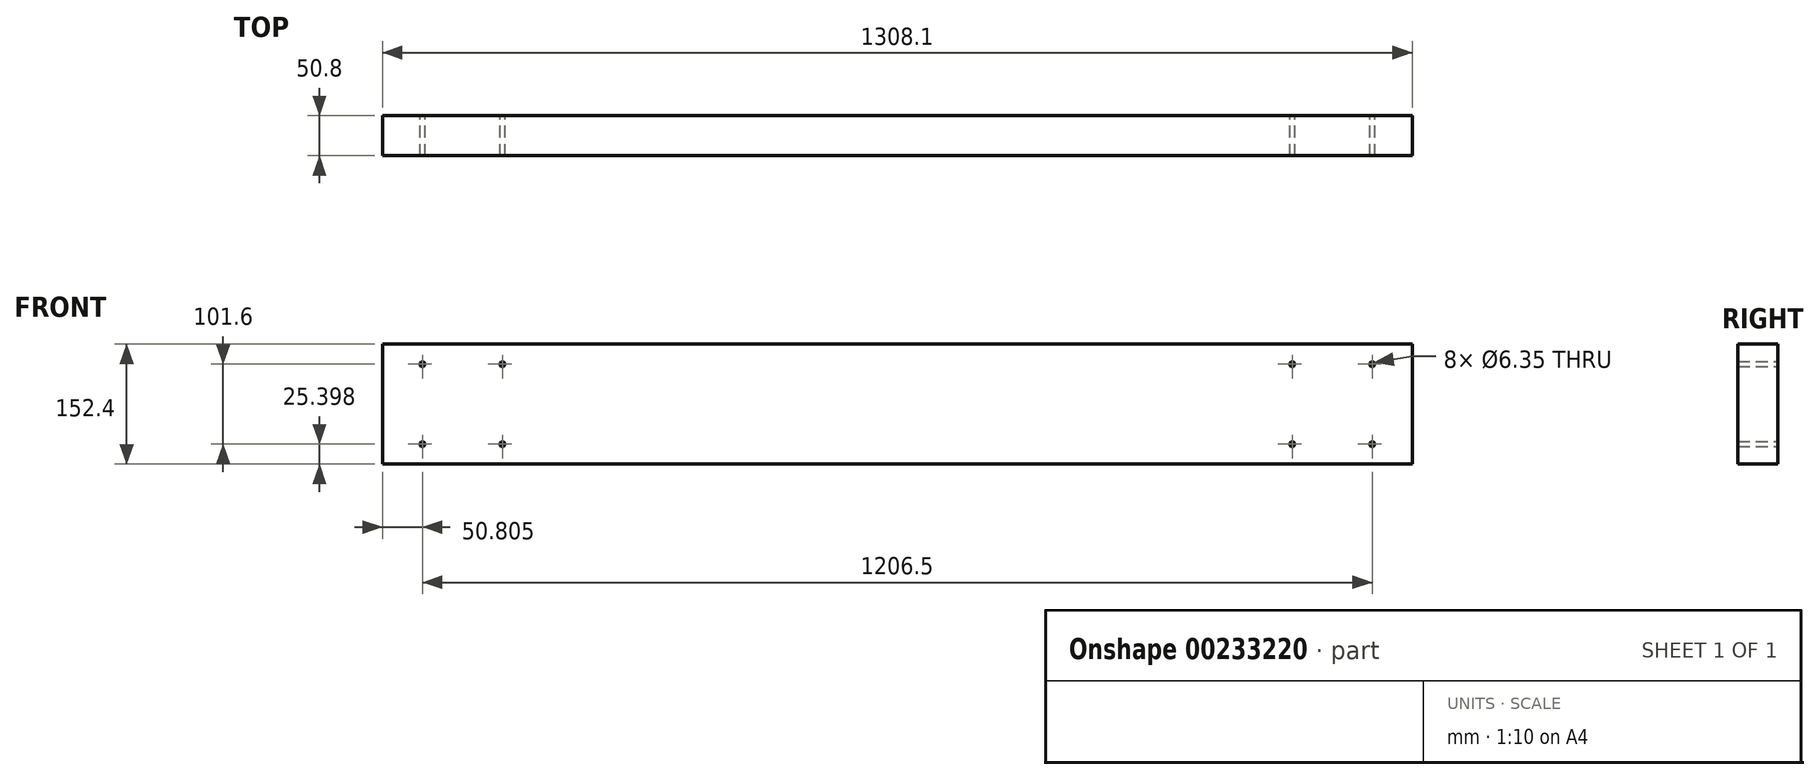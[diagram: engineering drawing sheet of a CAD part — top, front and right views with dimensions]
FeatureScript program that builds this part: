
annotation { "Feature Type Name" : "Feature", "Feature Type Description" : "" }
export const myFeature = defineFeature(function(context is Context, id is Id, definition is map)
    precondition{}
    {
        {
            var Q0;
            Q0=qCreatedBy(makeId("Front.planeOp"),FACE);
            var sketch = newSketch(context, id + "F0", { "sketchPlane" : qUnion([Q0])});
            skLineSegment(sketch, "E0.bottom", {"start": v(-533.62, -477.17) * mm, "end": v(774.48, -477.17) * mm});
            skLineSegment(sketch, "E0.top", {"start": v(-533.62, -629.57) * mm, "end": v(774.48, -629.57) * mm});
            skLineSegment(sketch, "E0.left", {"start": v(-533.62, -477.17) * mm, "end": v(-533.62, -629.57) * mm});
            skLineSegment(sketch, "E0.right", {"start": v(774.48, -477.17) * mm, "end": v(774.48, -629.57) * mm});
            skCircle(sketch, "E1", {"center": v(-482.82, -604.17) * mm, "radius": 3.18 * mm});
            skCircle(sketch, "E2", {"center": v(-482.82, -502.57) * mm, "radius": 3.18 * mm});
            skCircle(sketch, "E3", {"center": v(-381.22, -502.57) * mm, "radius": 3.17 * mm});
            skCircle(sketch, "E4", {"center": v(-381.22, -604.17) * mm, "radius": 3.18 * mm});
            skCircle(sketch, "E5", {"center": v(622.08, -604.17) * mm, "radius": 3.17 * mm});
            skCircle(sketch, "E6", {"center": v(723.68, -604.17) * mm, "radius": 3.17 * mm});
            skCircle(sketch, "E7", {"center": v(723.68, -502.57) * mm, "radius": 3.17 * mm});
            skCircle(sketch, "E8", {"center": v(622.08, -502.57) * mm, "radius": 3.17 * mm});
            skSolve(sketch);
        }
        {
            var Q0;
            Q0 = qSketchRegion(id + "F0", true);
            extrude(context, id + "F1", {"entities" : qUnion([Q0]), "depth" : 50.8 * mm});
        }
    });
